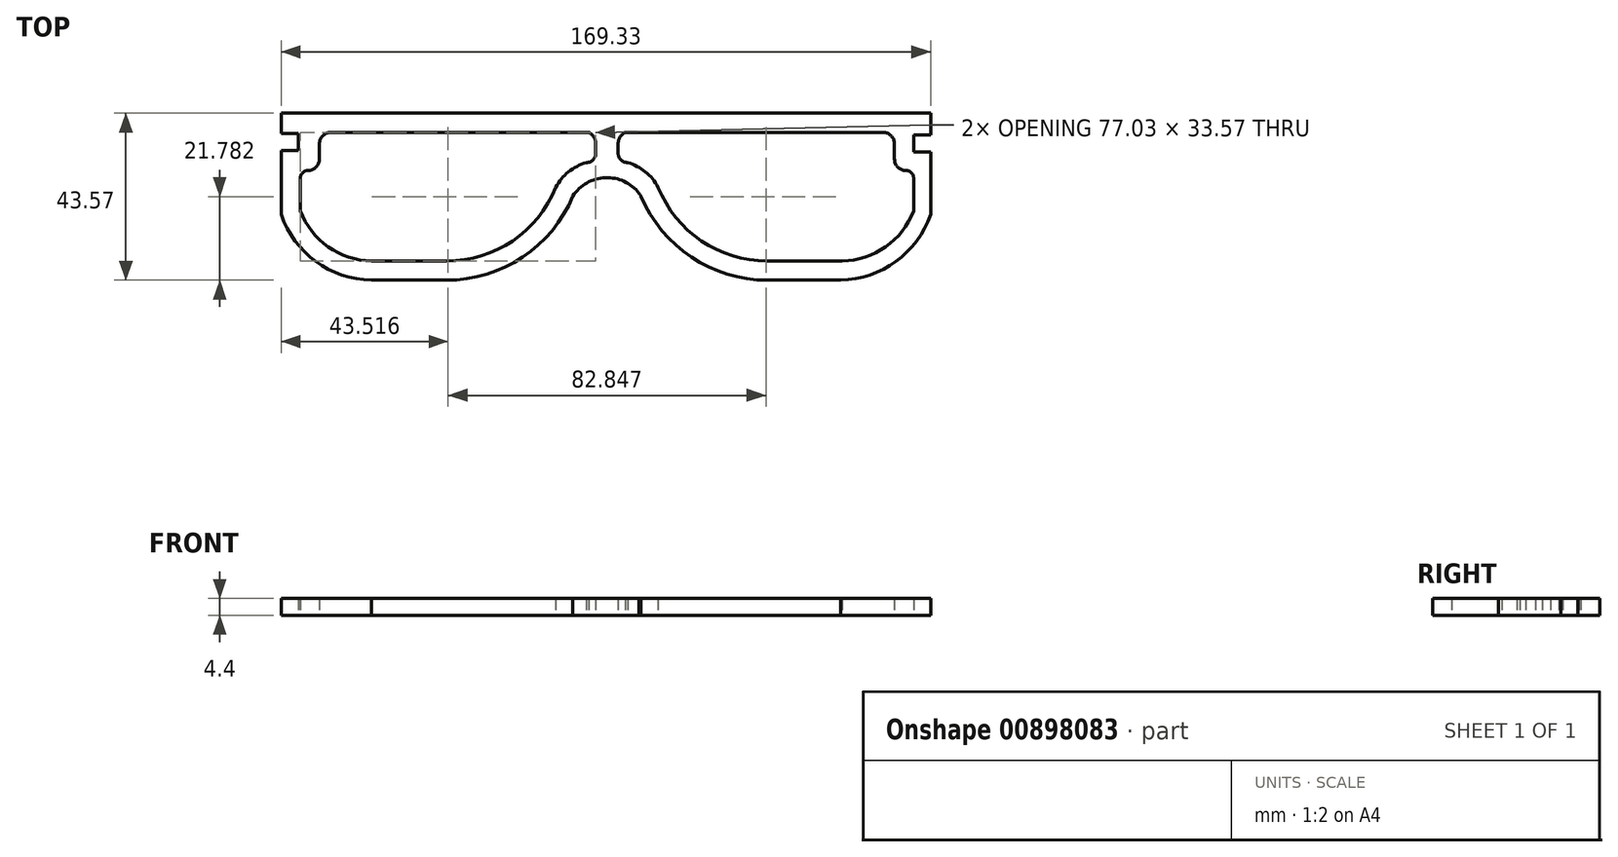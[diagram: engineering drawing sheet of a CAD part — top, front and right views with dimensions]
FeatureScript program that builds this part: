
annotation { "Feature Type Name" : "Feature", "Feature Type Description" : "" }
export const myFeature = defineFeature(function(context is Context, id is Id, definition is map)
    precondition{}
    {
        {
            var Q0;
            Q0=qCreatedBy(makeId("Top.planeOp"),FACE);
            var sketch = newSketch(context, id + "F0", { "sketchPlane" : qUnion([Q0])});
            skPoint(sketch, "E0.start.orphan", {"position": v(0, 75.12) * mm});
            skLineSegment(sketch, "E1", {"start": v(-75.5, -75.32) * mm, "end": v(-8.35, -75.32) * mm});
            skLineSegment(sketch, "E2", {"start": v(-78.5, -78.32) * mm, "end": v(-78.5, -82.28) * mm});
            skLineSegment(sketch, "E3", {"start": v(-83.5, -87.28) * mm, "end": v(-83.5, -95.85) * mm});
            skArc(sketch, "E4", {"start": v(-83.5, -95.85) * mm, "mid": v(-76.2, -105.2) * mm, "end": v(-64.93, -108.9) * mm});
            skLineSegment(sketch, "E5", {"start": v(-64.93, -108.9) * mm, "end": v(-45.35, -108.9) * mm});
            skArc(sketch, "E6", {"start": v(-45.35, -108.9) * mm, "mid": v(-28.18, -103.64) * mm, "end": v(-16.9, -89.67) * mm});
            skPoint(sketch, "E7.end.orphan", {"position": v(-45.35, -113.9) * mm});
            skLineSegment(sketch, "E8.0", {"start": v(80.82, -85.45) * mm, "end": v(80.82, -96.73) * mm});
            skArc(sketch, "E8.1", {"start": v(80.82, -96.73) * mm, "mid": v(71.76, -109.02) * mm, "end": v(57.3, -113.9) * mm});
            skLineSegment(sketch, "E8.2", {"start": v(57.3, -113.9) * mm, "end": v(38.23, -113.9) * mm});
            skArc(sketch, "E8.3", {"start": v(38.23, -113.9) * mm, "mid": v(18.47, -107.91) * mm, "end": v(5.34, -91.98) * mm});
            skArc(sketch, "E8.4", {"start": v(4.79, -91.23) * mm, "mid": v(5.07, -91.6) * mm, "end": v(5.34, -91.98) * mm});
            skLineSegment(sketch, "E8.6", {"start": v(-82.91, -70.32) * mm, "end": v(-3.57, -70.32) * mm});
            skLineSegment(sketch, "E8.7", {"start": v(76.38, -70.32) * mm, "end": v(-3.57, -70.32) * mm});
            skLineSegment(sketch, "E8.9", {"start": v(-88.5, -80) * mm, "end": v(-84.06, -80) * mm});
            skLineSegment(sketch, "E8.10", {"start": v(-88.5, -80) * mm, "end": v(-88.5, -96.73) * mm});
            skArc(sketch, "E8.11", {"start": v(-88.5, -96.73) * mm, "mid": v(-79.44, -109.01) * mm, "end": v(-64.98, -113.9) * mm});
            skLineSegment(sketch, "E8.12", {"start": v(-64.98, -113.9) * mm, "end": v(-45.35, -113.9) * mm});
            skArc(sketch, "E8.13", {"start": v(-45.35, -113.9) * mm, "mid": v(-25.58, -107.9) * mm, "end": v(-12.44, -91.96) * mm});
            skArc(sketch, "E8.14", {"start": v(4.79, -91.23) * mm, "mid": v(-4.02, -87.15) * mm, "end": v(-12.44, -91.96) * mm});
            skLineSegment(sketch, "E9", {"start": v(-84.06, -75.56) * mm, "end": v(-84.06, -80) * mm});
            skLineSegment(sketch, "E10", {"start": v(76.38, -70.32) * mm, "end": v(80.82, -70.32) * mm});
            skLineSegment(sketch, "E11", {"start": v(80.82, -75.28) * mm, "end": v(80.82, -70.32) * mm});
            skLineSegment(sketch, "E12", {"start": v(80.82, -85.45) * mm, "end": v(80.82, -80.45) * mm});
            skLineSegment(sketch, "E13", {"start": v(80.82, -80.45) * mm, "end": v(76.37, -80.45) * mm});
            skLineSegment(sketch, "E14", {"start": v(76.37, -80.45) * mm, "end": v(76.38, -76) * mm});
            skArc(sketch, "E15.filletArc", {"start": v(-8.96, -83.22) * mm, "mid": v(-7.3, -82.6) * mm, "end": v(-6.48, -81.04) * mm});
            skLineSegment(sketch, "E16", {"start": v(-6.48, -81.04) * mm, "end": v(-6.48, -81.04) * mm});
            skLineSegment(sketch, "E17", {"start": v(-6.48, -81.04) * mm, "end": v(-6.48, -78.28) * mm});
            skArc(sketch, "E18", {"start": v(-8.96, -83.22) * mm, "mid": v(-13.6, -85.63) * mm, "end": v(-16.9, -89.67) * mm});
            skArc(sketch, "E19.MirrorCS", {"start": v(9.6, -89.38) * mm, "mid": v(9.69, -89.52) * mm, "end": v(9.77, -89.67) * mm});
            skArc(sketch, "E20.trimOffspring", {"start": v(9.6, -89.38) * mm, "mid": v(9.7, -89.52) * mm, "end": v(9.8, -89.67) * mm});
            skArc(sketch, "E21.filletArc", {"start": v(-81.5, -85.28) * mm, "mid": v(-79.39, -84.4) * mm, "end": v(-78.5, -82.28) * mm});
            skArc(sketch, "E22.filletArc", {"start": v(-75.5, -75.32) * mm, "mid": v(-77.63, -76.2) * mm, "end": v(-78.5, -78.32) * mm});
            skArc(sketch, "E23", {"start": v(-81.5, -85.28) * mm, "mid": v(-82.92, -85.87) * mm, "end": v(-83.5, -87.28) * mm});
            skLineSegment(sketch, "E24", {"start": v(-3.57, -70.32) * mm, "end": v(-3.57, -87.14) * mm});
            skPoint(sketch, "E25.end.orphan", {"position": v(75.82, -95.85) * mm});
            skPoint(sketch, "E26.end.orphan", {"position": v(57.3, -108.9) * mm});
            skPoint(sketch, "E27.MirrorCS.start.orphan", {"position": v(1.82, -83.22) * mm});
            skPoint(sketch, "E28.start.orphan", {"position": v(1.82, -75.28) * mm});
            skLineSegment(sketch, "E29.MirrorCS", {"start": v(68.37, -75.32) * mm, "end": v(1.2, -75.32) * mm});
            skLineSegment(sketch, "E30.MirrorCS", {"start": v(-0.66, -81.04) * mm, "end": v(-0.66, -78.28) * mm});
            skArc(sketch, "E31.MirrorCS", {"start": v(1.82, -83.22) * mm, "mid": v(0.17, -82.6) * mm, "end": v(-0.66, -81.04) * mm});
            skArc(sketch, "E32.MirrorCS", {"start": v(1.82, -83.22) * mm, "mid": v(6.45, -85.63) * mm, "end": v(9.77, -89.67) * mm});
            skArc(sketch, "E33.MirrorCS", {"start": v(38.2, -108.9) * mm, "mid": v(21.04, -103.64) * mm, "end": v(9.77, -89.67) * mm});
            skLineSegment(sketch, "E34.MirrorCS", {"start": v(57.79, -108.9) * mm, "end": v(38.2, -108.9) * mm});
            skArc(sketch, "E35.MirrorCS", {"start": v(76.37, -95.85) * mm, "mid": v(69.05, -105.2) * mm, "end": v(57.79, -108.9) * mm});
            skLineSegment(sketch, "E36.MirrorCS", {"start": v(76.37, -87.28) * mm, "end": v(76.37, -95.85) * mm});
            skArc(sketch, "E37.MirrorCS", {"start": v(74.37, -85.28) * mm, "mid": v(75.78, -85.87) * mm, "end": v(76.37, -87.28) * mm});
            skArc(sketch, "E38.MirrorCS", {"start": v(74.37, -85.28) * mm, "mid": v(72.24, -84.4) * mm, "end": v(71.37, -82.28) * mm});
            skArc(sketch, "E39.MirrorCS", {"start": v(68.37, -75.32) * mm, "mid": v(70.49, -76.2) * mm, "end": v(71.37, -78.32) * mm});
            skLineSegment(sketch, "E40.MirrorCS", {"start": v(71.37, -78.32) * mm, "end": v(71.37, -82.28) * mm});
            skLineSegment(sketch, "E41.MirrorCS", {"start": v(-0.66, -81.04) * mm, "end": v(-0.66, -81.04) * mm});
            skPoint(sketch, "E42.MirrorP", {"position": v(38.2, -113.9) * mm});
            skArc(sketch, "E43.MirrorCS", {"start": v(38.2, -113.9) * mm, "mid": v(18.43, -107.9) * mm, "end": v(5.3, -91.96) * mm});
            skPoint(sketch, "E44.MirrorP", {"position": v(-8.96, -75.28) * mm});
            skLineSegment(sketch, "E45.MirrorCS", {"start": v(75.77, -70.32) * mm, "end": v(-3.57, -70.32) * mm});
            skPoint(sketch, "E46.MirrorP", {"position": v(-8.96, -83.22) * mm});
            skLineSegment(sketch, "E47.MirrorCS", {"start": v(57.3, -113.9) * mm, "end": v(38.2, -113.9) * mm});
            skPoint(sketch, "E48.end.orphan", {"position": v(-88.21, -70.94) * mm});
            skPoint(sketch, "E49.start.orphan", {"position": v(-88.5, -75.25) * mm});
            skPoint(sketch, "E50.MirrorCS.end.orphan", {"position": v(-84.06, -80.33) * mm});
            skLineSegment(sketch, "E51", {"start": v(-84.06, -75.56) * mm, "end": v(-88.5, -75.56) * mm});
            skLineSegment(sketch, "E52", {"start": v(-88.5, -75.56) * mm, "end": v(-88.5, -70.32) * mm});
            skLineSegment(sketch, "E53", {"start": v(-88.5, -70.32) * mm, "end": v(-82.91, -70.32) * mm});
            skPoint(sketch, "E54.MirrorCS.start.orphan", {"position": v(81.37, -75.25) * mm});
            skPoint(sketch, "E55.MirrorCS.start.orphan", {"position": v(76.92, -75.56) * mm});
            skPoint(sketch, "E56.MirrorCS.start.orphan", {"position": v(81.37, -80) * mm});
            skPoint(sketch, "E57.MirrorCS.start.orphan", {"position": v(81.37, -96.73) * mm});
            skPoint(sketch, "E58.orphan", {"position": v(57.84, -113.9) * mm});
            skLineSegment(sketch, "E59", {"start": v(76.38, -76) * mm, "end": v(80.82, -76) * mm});
            skLineSegment(sketch, "E60", {"start": v(80.82, -76) * mm, "end": v(80.82, -75.28) * mm});
            skPoint(sketch, "E61.MirrorCS.end.orphan", {"position": v(76.92, -80.33) * mm});
            skPoint(sketch, "E61.MirrorCS.start.orphan", {"position": v(76.92, -80) * mm});
            skPoint(sketch, "E62.MirrorCS.start.orphan", {"position": v(81.07, -70.94) * mm});
            skPoint(sketch, "E63.MirrorCS.end.orphan", {"position": v(-1.27, -78.32) * mm});
            skPoint(sketch, "E63.MirrorCS.start.orphan", {"position": v(1.2, -75.32) * mm});
            skArc(sketch, "E64", {"start": v(1.2, -75.32) * mm, "mid": v(-0.15, -76.53) * mm, "end": v(-0.66, -78.28) * mm});
            skPoint(sketch, "E65.MirrorCS.end.orphan", {"position": v(-5.87, -78.32) * mm});
            skArc(sketch, "E66", {"start": v(-6.48, -78.28) * mm, "mid": v(-6.99, -76.53) * mm, "end": v(-8.35, -75.32) * mm});
            skSolve(sketch);
        }
        {
            var Q0;
            Q0=makeQuery(id+"F0.imprint","IMPRINT",FACE,{"disambiguationData":[TD([[makeQuery(id+"F0.imprint","IMPRINT",EDGE,{"derivedFrom":sQuery(id+"F0.wireOp",EDGE,"E1")}),1.0]])]});
            var Q1;
            Q1=makeQuery(id+"F0.imprint","IMPRINT",FACE,{"disambiguationData":[TD([[makeQuery(id+"F0.imprint","IMPRINT",EDGE,{"derivedFrom":sQuery(id+"F0.wireOp",EDGE,"E8.0")}),-1.0]])]});
            extrude(context, id + "F1", {"entities" : qUnion([Q0, Q1]), "depth" : 4.4 * mm, "offsetDistance" : 25 * mm});
        }
    });
